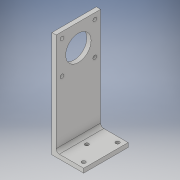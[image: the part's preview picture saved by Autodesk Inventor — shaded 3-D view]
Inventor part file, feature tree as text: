
AUTODESK INVENTOR PART (.ipt)
format: ipt  version: 2017 (Build 210142000, 142)  size: 147,456 bytes
history: native  units: in
note: dims shown in document units (in); Inventor stores cm internally (conversion verified against a paired STEP export)
features: extrude x3, sketch x3, fillet x1
ambient origin geometry x8: Origin, YZ Plane, XZ Plane, XY Plane, X Axis, Y Axis, Z Axis, Center Point
bodies: Solid1 (feature_tree)
feature tree (7):
  extrude  "Extrusion1"  Depth=1.1811in
  extrude  "Extrusion2"  Depth=1.0236in
  extrude  "Extrusion3"  Depth=3.7795in
  fillet  "Fillet1"  Radius=0.1378in
  sketch  "Sketch1"  dims[d0=3.937in d1=1.1811in]
  sketch  "Sketch2"  dims[d2=0.1575in d3=1.0236in]
  sketch  "Sketch3"  dims[d4=1.6535in d5=0.0in d6=3.7795in d7=0.1378in d8=0.2165in d9=0.2165in d10=0.1378in d11=0.2165in d12=0.2165in d14=0.1378in d15=0.1378in d16=1.2205in d17=1.2205in d18=0.2165in d19=0.2165in d20=0.9449in d21=0.8268in d22=0.6102in d23=0.1575in d24=0.0in d25=0.1378in d26=0.1378in d27=0.1378in d28=0.1969in d29=0.1969in d30=0.1969in d31=0.1969in d32=0.4724in d33=0.8268in d34=0.1575in d35=0.0in d36=0.1181in]
